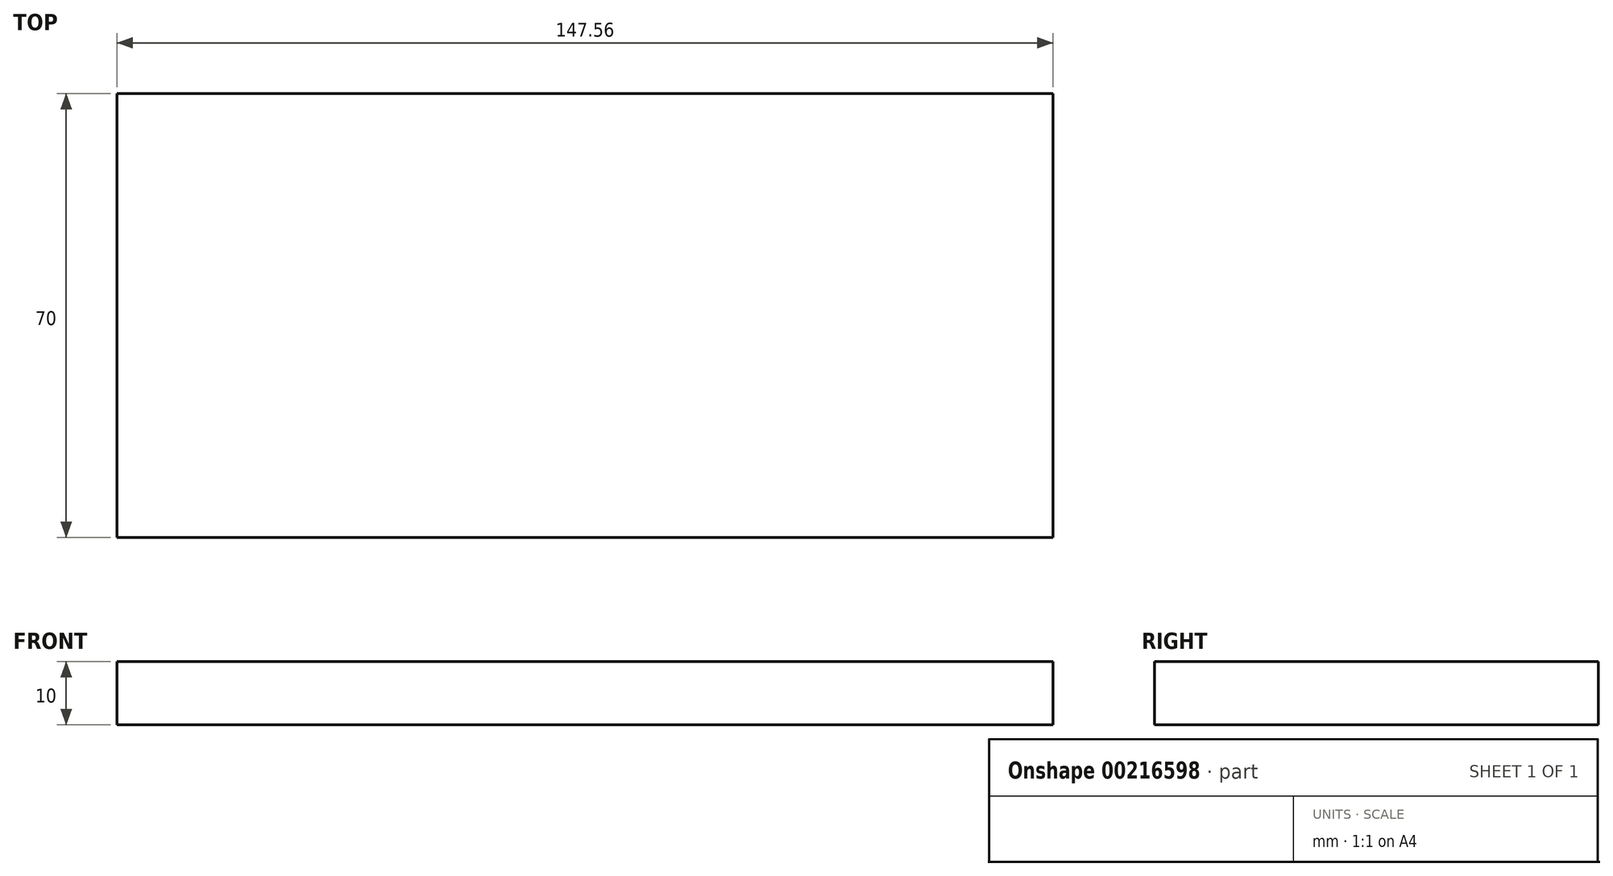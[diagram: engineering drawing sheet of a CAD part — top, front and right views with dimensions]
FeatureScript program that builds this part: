
annotation { "Feature Type Name" : "Feature", "Feature Type Description" : "" }
export const myFeature = defineFeature(function(context is Context, id is Id, definition is map)
    precondition{}
    {
        {
            var Q0;
            Q0=qCreatedBy(makeId("Top.planeOp"),FACE);
            var sketch = newSketch(context, id + "F0", { "sketchPlane" : qUnion([Q0])});
            skLineSegment(sketch, "E0.bottom", {"start": v(73.78, 35) * mm, "end": v(-73.78, 35) * mm});
            skLineSegment(sketch, "E0.top", {"start": v(73.78, -35) * mm, "end": v(-73.78, -35) * mm});
            skLineSegment(sketch, "E0.left", {"start": v(73.78, 35) * mm, "end": v(73.78, -35) * mm});
            skLineSegment(sketch, "E0.right", {"start": v(-73.78, 35) * mm, "end": v(-73.78, -35) * mm});
            skPoint(sketch, "E0.middle", {"position": v(0, 0) * mm});
            skSolve(sketch);
        }
        {
            var Q0;
            Q0=makeQuery(id+"F0.imprint","IMPRINT",FACE,{"disambiguationData":[TD([[makeQuery(id+"F0.imprint","IMPRINT",EDGE,{"derivedFrom":sQuery(id+"F0.wireOp",EDGE,"E0.bottom")}),1.0]])]});
            extrude(context, id + "F1", {"entities" : qUnion([Q0]), "depth" : 10 * mm});
        }
    });
